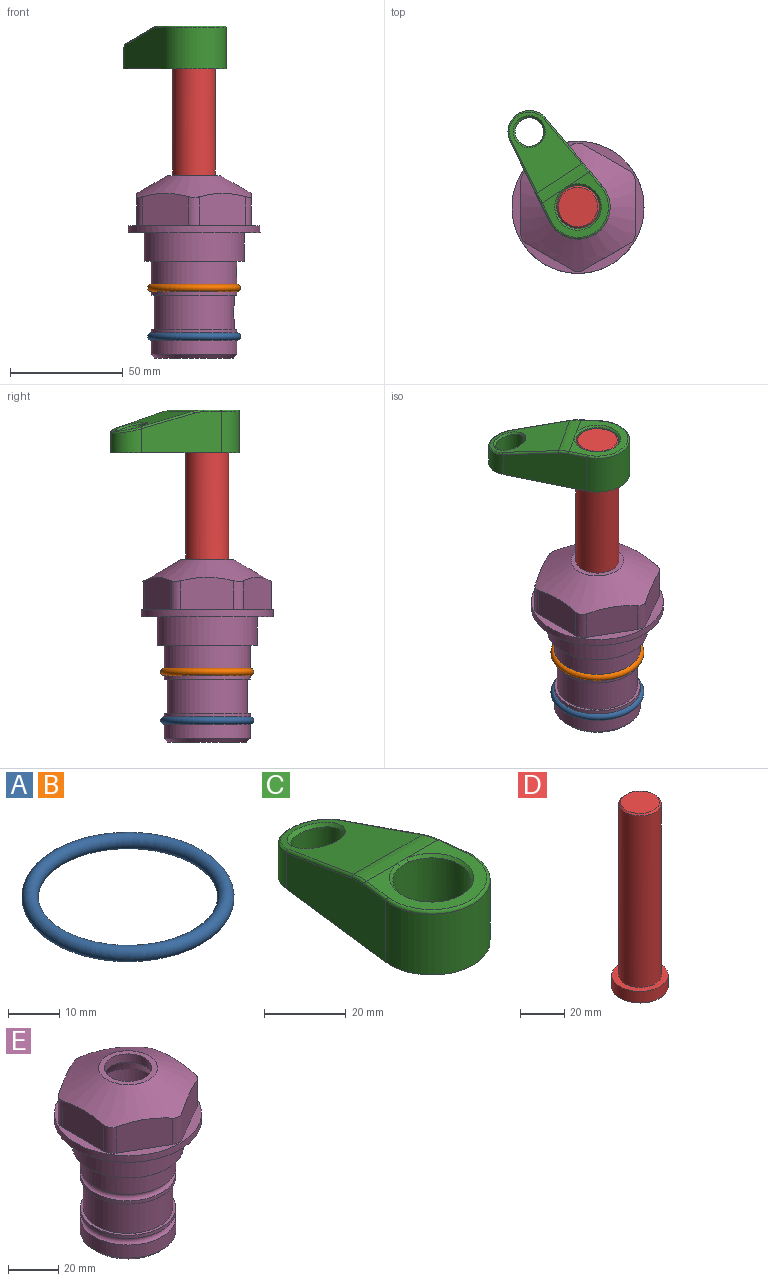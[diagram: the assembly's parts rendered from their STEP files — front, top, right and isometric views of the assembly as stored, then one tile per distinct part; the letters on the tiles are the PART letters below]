
ASSEMBLY  parts=5 mates=4
PART A: 1 faces, bbox 44.7x44.7x3.2 mm
  f0: torus R=19.05mm, axis (0,0,1), area 1193.9mm2
PART B: same geometry as A
PART C: 31 faces, bbox 31.7x65.5x19.8 mm
  f0: plane 39.12x18.26mm, normal (0.99,0.12,0), area 612.2mm2, adj f1,f4,f7,f11,f13,f15
  f1: cylinder r=9.53mm len=18.91mm, axis (0,0,-1), area 296.1mm2, adj f0,f2,f7,f17
  f2: plane 39.12x18.26mm, normal (-0.99,0.12,0), area 612.2mm2, adj f1,f4,f7,f12,f14,f16
  f3: cylinder r=6.35mm len=12.7mm, axis (0,0,-1), area 362.4mm2, adj f7,f18
  f4: cylinder r=14.29mm len=28.58mm, axis (0,0,-1), area 882.2mm2, adj f0,f2,f7,f10
  f5: cylinder r=9.53mm len=19.05mm, axis (0,0,-1), area 1092.6mm2, adj f7,f19,f20
  f6: plane 26.99x23.69mm, normal (0,0,1), area 216.2mm2, adj f9,f10,f11,f12,f19
  f7: plane 63.5x28.58mm, normal (0,0,-1), area 661.8mm2, adj f0,f1,f2,f3,f4,f5,f22,f23
  f8: plane 33.52x23.6mm, normal (0,0.26,0.97), area 486mm2, adj f9,f15,f16,f17,f18
  f9: cylinder r=19.05mm len=24.72mm, axis (1,0,0), area 120.4mm2, adj f6,f8,f13,f14,f20
  f10: torus R=13.49mm, axis (0,0,1), area 59mm2, adj f4,f6,f11,f12
  f11: cylinder r=0.79mm len=8.67mm, axis (0.12,-0.99,0), area 10.8mm2, adj f0,f6,f10,f13
  f12: cylinder r=0.79mm len=8.67mm, axis (0.12,0.99,0), area 10.8mm2, adj f2,f6,f10,f14
  f13: bspline ~4.95x1.42mm, area 6.1mm2, adj f0,f9,f11,f15
  f14: bspline ~4.95x1.42mm, area 6.1mm2, adj f2,f9,f12,f16
  f15: cylinder r=0.79mm len=25.95mm, axis (0.12,-0.96,0.26), area 32.9mm2, adj f0,f8,f13,f17
  f16: cylinder r=0.79mm len=25.95mm, axis (0.12,0.96,-0.26), area 32.9mm2, adj f2,f8,f14,f17
  f17: bspline ~18.91x8.38mm, area 30mm2, adj f1,f8,f15,f16
  f18: bspline ~14.29x14.29mm, area 48.3mm2, adj f3,f8
  f19: cone r=9.53mm half-angle=45deg, axis (0,0,1), area 66.5mm2, adj f5,f6,f20
  f20: bspline ~3.22x0.96mm, area 3.5mm2, adj f5,f9,f19
  f21: plane 2.75x2.72mm, normal (0,0,-1), area 2.9mm2, adj f23,f25,f28
  f22: plane 23.05x15.88mm, normal (-0.99,-0.12,0), area 323.6mm2, adj f7,f25,f26,f27,f28,f29
  f23: plane 23.05x15.88mm, normal (0.99,-0.12,0), area 323.6mm2, adj f7,f21,f25,f27,f28,f30
  f24: cylinder r=9.53mm len=10.69mm, axis (0,0,-1), area 114.7mm2, adj f7,f27,f29,f30
  f25: cylinder r=12.7mm len=20.59mm, axis (0,0,-1), area 381.1mm2, adj f7,f21,f22,f23,f26,f28
  f26: plane 2.75x2.72mm, normal (0,0,-1), area 2.9mm2, adj f22,f25,f28
  f27: plane 19.72x18.37mm, normal (0,-0.26,-0.97), area 291.8mm2, adj f22,f23,f24,f28,f29,f30
  f28: cylinder r=15.88mm len=19.92mm, axis (1,0,0), area 54.8mm2, adj f21,f22,f23,f25,f26,f27
  f29: cylinder r=1.59mm len=11mm, axis (0,0,-1), area 34.7mm2, adj f7,f22,f24,f27
  f30: cylinder r=1.59mm len=11mm, axis (0,0,-1), area 34.7mm2, adj f7,f23,f24,f27
PART D: 6 faces, bbox 25.4x25.4x101.6 mm
  f0: plane 17.46x17.46mm, normal (0,0,1), area 239.5mm2, adj f5
  f1: plane 25.4x25.4mm, normal (0,0,-1), area 506.7mm2, adj f2
  f2: cylinder r=12.7mm len=25.4mm, axis (0,0,1), area 506.7mm2, adj f1,f3
  f3: plane 25.4x25.4mm, normal (0,0,1), area 221.7mm2, adj f2,f4
  f4: cylinder r=9.53mm len=94.46mm, axis (0,0,1), area 5653mm2, adj f3,f5
  f5: cone r=8.73mm half-angle=45deg, axis (0,0,-1), area 64.4mm2, adj f0,f4
PART E: 36 faces, bbox 58.7x58.7x81 mm
  f0: cylinder r=17.78mm len=35.56mm, axis (0,0,1), area 1670.8mm2, adj f23,f24,f31
  f1: cylinder r=19.05mm len=38.1mm, axis (0,0,1), area 1191.9mm2, adj f26,f27,f30
  f2: plane 58.66x58.66mm, normal (0,0,-1), area 1150.6mm2, adj f3,f28
  f3: cylinder r=29.33mm len=58.66mm, axis (0,0,-1), area 585.1mm2, adj f2,f4
  f4: plane 58.66x58.66mm, normal (0,0,1), area 475.9mm2, adj f3,f5,f6,f7,f8,f9,f10,f11
  f5: plane 20.32x14.34mm, normal (-0.5,0.87,0), area 324.4mm2, adj f4,f15,f16,f17
  f6: plane 20.32x14.34mm, normal (0.5,0.87,0), area 324.4mm2, adj f4,f14,f15,f17
  f7: plane 23.48x14.34mm, normal (1,0,0), area 324.4mm2, adj f4,f13,f14,f17
  f8: plane 20.32x14.34mm, normal (0.5,-0.87,0), area 324.4mm2, adj f4,f12,f13,f17
  f9: plane 20.32x14.34mm, normal (-0.5,-0.87,0), area 324.4mm2, adj f4,f11,f12,f17
  f10: plane 23.48x14.34mm, normal (-1,0,0), area 324.4mm2, adj f4,f11,f16,f17
  f11: cylinder r=5.08mm len=12.85mm, axis (0,0,-1), area 67.2mm2, adj f4,f9,f10,f17
  f12: cylinder r=5.08mm len=12.85mm, axis (0,0,-1), area 67.2mm2, adj f4,f8,f9,f17
  f13: cylinder r=5.08mm len=12.85mm, axis (0,0,-1), area 67.2mm2, adj f4,f7,f8,f17
  f14: cylinder r=5.08mm len=12.85mm, axis (0,0,-1), area 67.2mm2, adj f4,f6,f7,f17
  f15: cylinder r=5.08mm len=12.85mm, axis (0,0,-1), area 67.2mm2, adj f4,f5,f6,f17
  f16: cylinder r=5.08mm len=12.85mm, axis (0,0,-1), area 67.2mm2, adj f4,f5,f10,f17
  f17: cone r=11.73mm half-angle=60deg, axis (0,0,-1), area 2071.8mm2, adj f5,f6,f7,f8,f9,f10,f11,f12
  f18: plane 23.46x23.46mm, normal (0,0,1), area 147.4mm2, adj f17,f35
  f19: plane 34.93x34.93mm, normal (0,0,-1), area 958mm2, adj f29
  f20: cylinder r=19.05mm len=38.1mm, axis (0,0,1), area 760.1mm2, adj f21,f29
  f21: torus R=19.05mm, axis (0,0,1), area 565.3mm2, adj f20,f22
  f22: cylinder r=19.05mm len=38.1mm, axis (0,0,1), area 190mm2, adj f21,f23
  f23: plane 38.1x38.1mm, normal (0,0,1), area 146.9mm2, adj f0,f22
  f24: plane 38.1x38.1mm, normal (0,0,-1), area 146.9mm2, adj f0,f25
  f25: cylinder r=19.05mm len=38.1mm, axis (0,0,1), area 190mm2, adj f24,f26
  f26: torus R=19.05mm, axis (0,0,1), area 565.3mm2, adj f1,f25
  f27: plane 44.45x44.45mm, normal (0,0,-1), area 411.7mm2, adj f1,f28
  f28: cylinder r=22.23mm len=44.45mm, axis (0,0,1), area 1773.5mm2, adj f2,f27
  f29: cone r=19.05mm half-angle=45deg, axis (0,0,1), area 257.5mm2, adj f19,f20
  f30: cylinder r=3.17mm len=6.75mm, axis (-1,0,0), area 128mm2, adj f1,f33
  f31: cylinder r=3.17mm len=6.35mm, axis (-1,0,0), area 102.5mm2, adj f0,f33
  f32: plane 25.4x25.4mm, normal (0,0,1), area 506.7mm2, adj f33
  f33: cylinder r=12.7mm len=66.42mm, axis (0,0,-1), area 5236.2mm2, adj f30,f31,f32,f34
  f34: cone r=9.53mm half-angle=30deg, axis (0,0,-1), area 443.4mm2, adj f33,f35
  f35: cylinder r=9.53mm len=19.05mm, axis (0,0,-1), area 240.9mm2, adj f18,f34
PLACE A t=(0,0,-21.59)mm
PLACE B at identity
PLACE C rot(axis=(0,0,1),32.9deg) t=(0,0,28.35)mm
PLACE D rot(axis=(0,0,1),32.9deg) t=(0,0,27.55)mm
PLACE E at identity fixed
MATE fastened C.f4 <-> D.f2  axis (0,0,-1) through (0,0,91.05)mm
MATE fastened B.f0 <-> E.f0  axis (0,0,1) through (0,0,-24.51)mm
MATE fastened A.f0 <-> E.f0  axis (0,0,1) through (0,0,-46.1)mm
MATE cylindrical E.f0 <-> D.f2  axis (0,0,1) through (0,0,-50.55)mm
